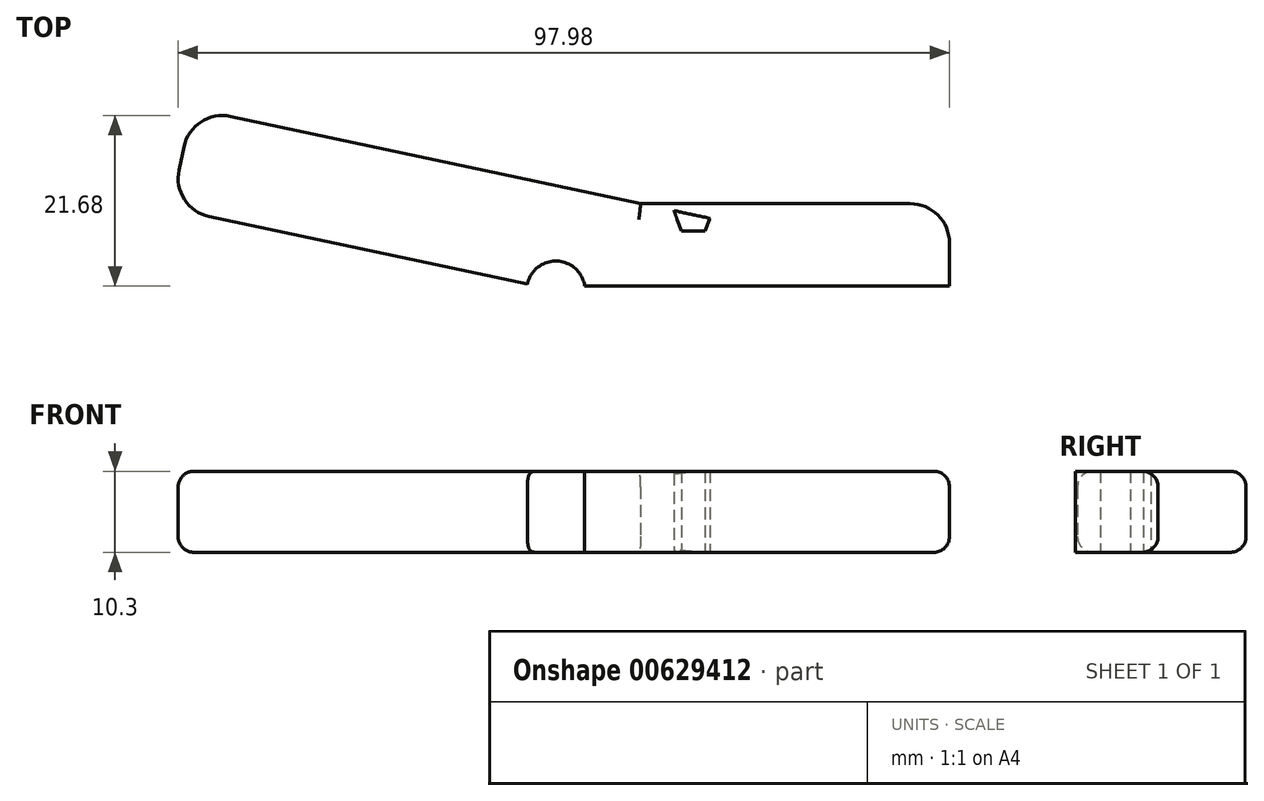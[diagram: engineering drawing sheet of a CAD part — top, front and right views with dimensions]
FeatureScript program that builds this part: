
annotation { "Feature Type Name" : "Feature", "Feature Type Description" : "" }
export const myFeature = defineFeature(function(context is Context, id is Id, definition is map)
    precondition{}
    {
        {
            var Q0;
            Q0=qCreatedBy(makeId("Top.planeOp"),FACE);
            var sketch = newSketch(context, id + "F0", { "sketchPlane" : qUnion([Q0])});
            skArc(sketch, "E0", {"start": v(15.5, -11) * mm, "mid": v(16.57, -9.3) * mm, "end": v(17.46, -7.5) * mm});
            skLineSegment(sketch, "E1.bottom", {"start": v(15.96, 7.5) * mm, "end": v(18.96, 7.5) * mm});
            skLineSegment(sketch, "E1.top", {"start": v(15.96, -7.5) * mm, "end": v(18.96, -7.5) * mm});
            skLineSegment(sketch, "E1.left", {"start": v(15.96, 0.5) * mm, "end": v(15.96, -0.5) * mm});
            skLineSegment(sketch, "E1.right", {"start": v(18.96, 0.5) * mm, "end": v(18.96, -1.28) * mm});
            skPoint(sketch, "E2", {"position": v(17.46, 7.5) * mm});
            skArc(sketch, "E3", {"start": v(3.67, 0.5) * mm, "mid": v(0.14, 3.7) * mm, "end": v(-3.62, 0.77) * mm});
            skLineSegment(sketch, "E4.bottom", {"start": v(3.67, 0.5) * mm, "end": v(50, 0.5) * mm});
            skLineSegment(sketch, "E4.top", {"start": v(18.96, -0.5) * mm, "end": v(19, -0.5) * mm});
            skLineSegment(sketch, "E4.left", {"start": v(0, 0.5) * mm, "end": v(0, -0.5) * mm});
            skLineSegment(sketch, "E4.right", {"start": v(50, 0.5) * mm, "end": v(50, -0.5) * mm});
            skLineSegment(sketch, "E5.bottom", {"start": v(50, -11) * mm, "end": v(0, -11) * mm});
            skLineSegment(sketch, "E5.top", {"start": v(50, 11) * mm, "end": v(10.78, 11) * mm});
            skLineSegment(sketch, "E5.left", {"start": v(50, -11) * mm, "end": v(50, 11) * mm});
            skLineSegment(sketch, "E5.right", {"start": v(0, -3.7) * mm, "end": v(0, 0.5) * mm});
            skLineSegment(sketch, "E6", {"start": v(-3.62, 0.77) * mm, "end": v(-48.9, 10.4) * mm});
            skLineSegment(sketch, "E7", {"start": v(-48.9, 10.4) * mm, "end": v(-46.2, 23.11) * mm});
            skLineSegment(sketch, "E8", {"start": v(-46.2, 23.11) * mm, "end": v(15.01, 10.1) * mm});
            skLineSegment(sketch, "E9", {"start": v(18.96, 7.5) * mm, "end": v(19.55, 9.13) * mm});
            skLineSegment(sketch, "E10", {"start": v(15.96, 7.5) * mm, "end": v(15.01, 10.1) * mm});
            skLineSegment(sketch, "E11.trimOffspring", {"start": v(10.78, 11) * mm, "end": v(19.55, 9.13) * mm});
            skPoint(sketch, "E12.orphan", {"position": v(0, 8.5) * mm});
            skSolve(sketch);
        }
        {
            var Q0;
            Q0=makeQuery(id+"F0.imprint","IMPRINT",FACE,{"disambiguationData":[TD([[makeQuery(id+"F0.imprint","IMPRINT",EDGE,{"derivedFrom":sQuery(id+"F0.wireOp",EDGE,"E1.bottom")}),-1.0]])]});
            extrude(context, id + "F1", {"entities" : qUnion([Q0]), "depth" : 10.3 * mm, "offsetDistance" : 25 * mm});
        }
        {
            var Q0;
            Q0=makeQuery(id+"F1.opExtrude","SWEPT_EDGE",EDGE,{"disambiguationData":[OSD([sQuery(id+"F0.wireOp",EDGE,"E5.top"),sQuery(id+"F0.wireOp",EDGE,"E5.left")])]});
            var Q1;
            Q1=makeQuery(id+"F1.opExtrude","SWEPT_EDGE",EDGE,{"disambiguationData":[OSD([sQuery(id+"F0.wireOp",EDGE,"E7"),sQuery(id+"F0.wireOp",EDGE,"E8")])]});
            var Q2;
            Q2=makeQuery(id+"F1.opExtrude","SWEPT_EDGE",EDGE,{"disambiguationData":[OSD([sQuery(id+"F0.wireOp",EDGE,"E6"),sQuery(id+"F0.wireOp",EDGE,"E7")])]});
            fillet(context, id + "F2", {"entities" : qUnion([Q0, Q1, Q2]), "radius" : 5 * mm, "tangentPropagation" : true, "allowEdgeOverflow" : false});
        }
        {
            var Q0;
            Q0=makeQuery(id+"F1.opExtrude","CAP_EDGE",EDGE,{"disambiguationData":[OSD([sQuery(id+"F0.wireOp",EDGE,"E8")])],"isStart":false});
            var Q1;
            Q1=makeQuery(id+"F1.opExtrude","CAP_EDGE",EDGE,{"disambiguationData":[OSD([sQuery(id+"F0.wireOp",EDGE,"E5.top")])],"isStart":false});
            var Q2;
            Q2=makeQuery(id+"F1.opExtrude","CAP_EDGE",EDGE,{"disambiguationData":[OSD([sQuery(id+"F0.wireOp",EDGE,"E5.top")])],"isStart":true});
            var Q3;
            Q3=makeQuery(id+"F1.opExtrude","CAP_EDGE",EDGE,{"disambiguationData":[OSD([sQuery(id+"F0.wireOp",EDGE,"E8")])],"isStart":true});
            fillet(context, id + "F3", {"entities" : qUnion([Q0, Q1, Q2, Q3]), "radius" : 2 * mm, "tangentPropagation" : true, "allowEdgeOverflow" : false});
        }
    });
